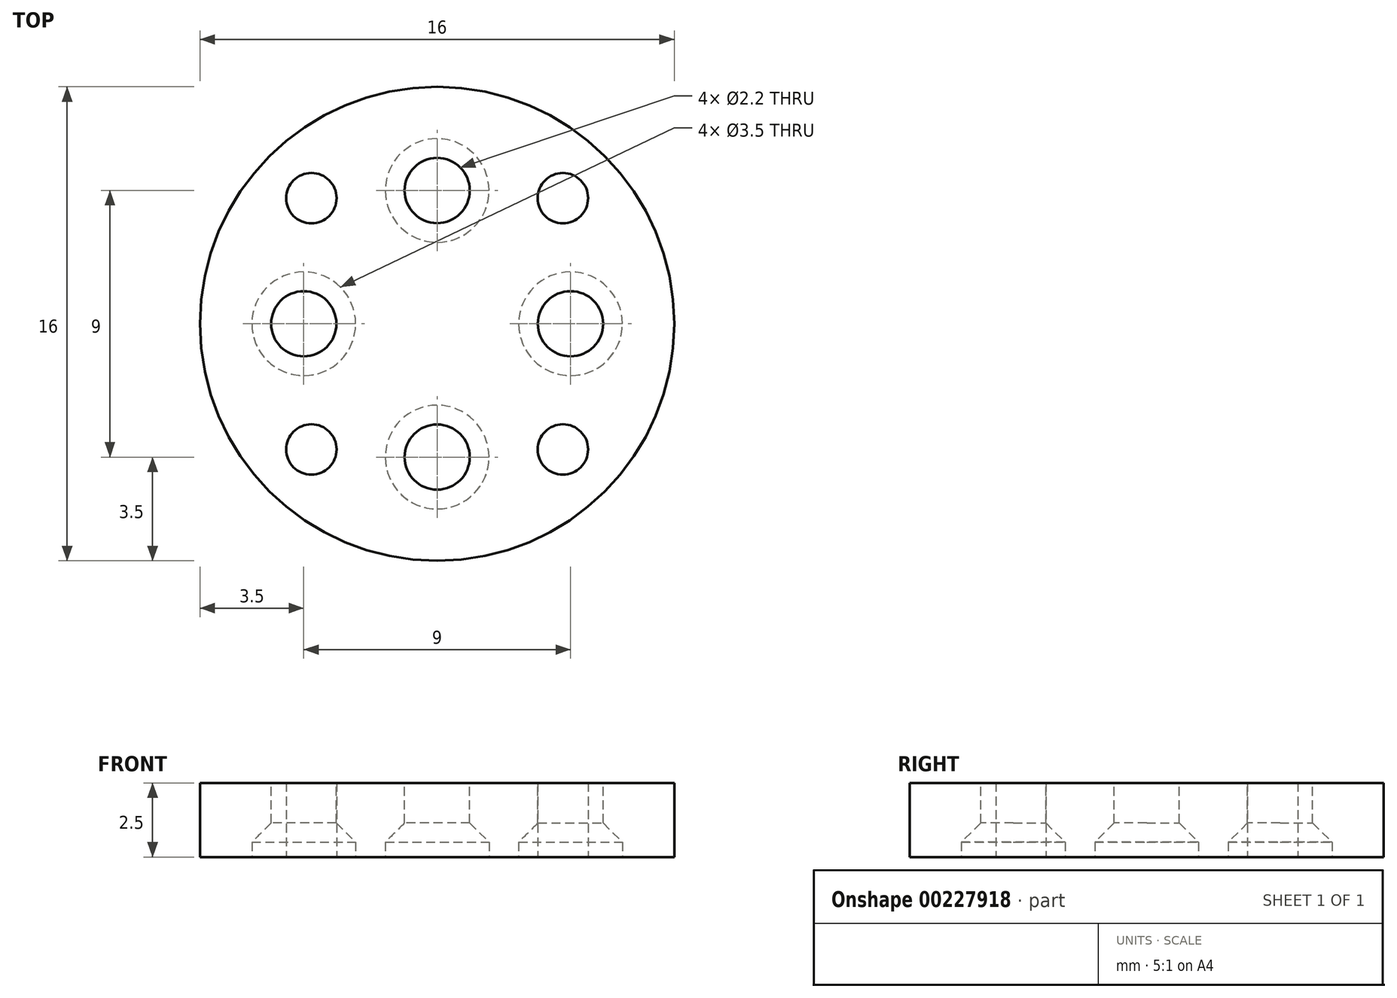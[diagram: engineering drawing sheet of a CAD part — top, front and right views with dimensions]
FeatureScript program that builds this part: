
annotation { "Feature Type Name" : "Feature", "Feature Type Description" : "" }
export const myFeature = defineFeature(function(context is Context, id is Id, definition is map)
    precondition{}
    {
        {
            var Q0;
            Q0=qCreatedBy(makeId("Top.planeOp"),FACE);
            var sketch = newSketch(context, id + "F0", { "sketchPlane" : qUnion([Q0])});
            skCircle(sketch, "E0", {"center": v(0, 0) * mm, "radius": 8 * mm});
            skSolve(sketch);
        }
        {
            var Q0;
            Q0=makeQuery(id+"F0.imprint","IMPRINT",FACE,{"disambiguationData":[TD([[makeQuery(id+"F0.imprint","IMPRINT",EDGE,{"derivedFrom":sQuery(id+"F0.wireOp",EDGE,"E0")}),1.0]])]});
            extrude(context, id + "F1", {"entities" : qUnion([Q0]), "depth" : 2.5 * mm});
        }
        {
            var Q0;
            Q0=makeQuery(id+"F1.opExtrude","CAP_FACE",FACE,{"disambiguationData":[OSD([sQuery(id+"F0.wireOp",EDGE,"E0")])],"isStart":false});
            var sketch = newSketch(context, id + "F2", { "sketchPlane" : qUnion([Q0])});
            skCircle(sketch, "E1", {"center": v(0, 4.5) * mm, "radius": 1.1 * mm});
            skCircle(sketch, "E2.1.0", {"center": v(-4.5, 0) * mm, "radius": 1.1 * mm});
            skCircle(sketch, "E2.2.0", {"center": v(0, -4.5) * mm, "radius": 1.1 * mm});
            skCircle(sketch, "E2.3.0", {"center": v(4.5, 0) * mm, "radius": 1.1 * mm});
            skPoint(sketch, "E2.center", {"position": v(0, 0) * mm});
            skSolve(sketch);
        }
        {
            var Q0;
            Q0 = qSketchRegion(id + "F2", true);
            extrude(context, id + "F3", {"entities" : qUnion([Q0]), "operationType" : NewBodyOperationType.REMOVE, "endBound" : BoundingType.THROUGH_ALL, "oppositeDirection" : true, "depth" : 25 * mm});
        }
        {
            var Q0;
            Q0=makeQuery(id+"F1.opExtrude","CAP_FACE",FACE,{"disambiguationData":[OSD([sQuery(id+"F0.wireOp",EDGE,"E0")])],"isStart":true});
            var sketch = newSketch(context, id + "F4", { "sketchPlane" : qUnion([Q0])});
            skCircle(sketch, "E3", {"center": v(4.24, 4.24) * mm, "radius": 0.85 * mm});
            skCircle(sketch, "E4.1.0", {"center": v(-4.24, 4.24) * mm, "radius": 0.85 * mm});
            skCircle(sketch, "E4.2.0", {"center": v(-4.24, -4.24) * mm, "radius": 0.85 * mm});
            skCircle(sketch, "E4.3.0", {"center": v(4.24, -4.24) * mm, "radius": 0.85 * mm});
            skPoint(sketch, "E4.center", {"position": v(0, 0) * mm});
            skLineSegment(sketch, "E5", {"start": v(0, 0) * mm, "end": v(4.24, 4.24) * mm, "construction": true});
            skSolve(sketch);
        }
        {
            var Q0;
            Q0=makeQuery(id+"F4.imprint","IMPRINT",FACE,{"disambiguationData":[TD([[makeQuery(id+"F4.imprint","IMPRINT",EDGE,{"derivedFrom":sQuery(id+"F4.wireOp",EDGE,"E4.1.0")}),1.0]])]});
            var Q1;
            Q1=makeQuery(id+"F4.imprint","IMPRINT",FACE,{"disambiguationData":[TD([[makeQuery(id+"F4.imprint","IMPRINT",EDGE,{"derivedFrom":sQuery(id+"F4.wireOp",EDGE,"E3")}),1.0]])]});
            var Q2;
            Q2=makeQuery(id+"F4.imprint","IMPRINT",FACE,{"disambiguationData":[TD([[makeQuery(id+"F4.imprint","IMPRINT",EDGE,{"derivedFrom":sQuery(id+"F4.wireOp",EDGE,"E4.3.0")}),1.0]])]});
            var Q3;
            Q3=makeQuery(id+"F4.imprint","IMPRINT",FACE,{"disambiguationData":[TD([[makeQuery(id+"F4.imprint","IMPRINT",EDGE,{"derivedFrom":sQuery(id+"F4.wireOp",EDGE,"E4.2.0")}),1.0]])]});
            extrude(context, id + "F5", {"entities" : qUnion([Q0, Q1, Q2, Q3]), "operationType" : NewBodyOperationType.REMOVE, "endBound" : BoundingType.THROUGH_ALL, "oppositeDirection" : true, "depth" : 25 * mm});
        }
        {
            var Q0;
            Q0=makeQuery(id+"F1.opExtrude","CAP_FACE",FACE,{"disambiguationData":[OSD([sQuery(id+"F0.wireOp",EDGE,"E0")])],"isStart":false});
            var sketch = newSketch(context, id + "F6", { "sketchPlane" : qUnion([Q0])});
            skArc(sketch, "E6", {"start": v(-4.24, 2.4) * mm, "mid": v(-2.93, 2.93) * mm, "end": v(-2.4, 4.24) * mm});
            skLineSegment(sketch, "E7", {"start": v(-2.4, 7.63) * mm, "end": v(-2.4, 4.24) * mm});
            skLineSegment(sketch, "E8", {"start": v(-7.63, 2.4) * mm, "end": v(-4.24, 2.4) * mm});
            skLineSegment(sketch, "E9", {"start": v(-4.24, 4.24) * mm, "end": v(0, 0) * mm, "construction": true});
            skArc(sketch, "E10.0", {"start": v(-2.4, 7.63) * mm, "mid": v(-5.66, 5.66) * mm, "end": v(-7.63, 2.4) * mm});
            skLineSegment(sketch, "E11.1.0", {"start": v(-2.4, -7.63) * mm, "end": v(-2.4, -4.24) * mm});
            skArc(sketch, "E11.1.1", {"start": v(-7.63, -2.4) * mm, "mid": v(-5.66, -5.66) * mm, "end": v(-2.4, -7.63) * mm});
            skLineSegment(sketch, "E11.1.2", {"start": v(-7.63, -2.4) * mm, "end": v(-4.24, -2.4) * mm});
            skArc(sketch, "E11.1.3", {"start": v(-2.4, -4.24) * mm, "mid": v(-2.93, -2.93) * mm, "end": v(-4.24, -2.4) * mm});
            skLineSegment(sketch, "E11.2.0", {"start": v(7.63, -2.4) * mm, "end": v(4.24, -2.4) * mm});
            skArc(sketch, "E11.2.1", {"start": v(2.4, -7.63) * mm, "mid": v(5.66, -5.66) * mm, "end": v(7.63, -2.4) * mm});
            skLineSegment(sketch, "E11.2.2", {"start": v(2.4, -7.63) * mm, "end": v(2.4, -4.24) * mm});
            skArc(sketch, "E11.2.3", {"start": v(4.24, -2.4) * mm, "mid": v(2.93, -2.93) * mm, "end": v(2.4, -4.24) * mm});
            skLineSegment(sketch, "E11.3.0", {"start": v(2.4, 7.63) * mm, "end": v(2.4, 4.24) * mm});
            skArc(sketch, "E11.3.1", {"start": v(7.63, 2.4) * mm, "mid": v(5.66, 5.66) * mm, "end": v(2.4, 7.63) * mm});
            skLineSegment(sketch, "E11.3.2", {"start": v(7.63, 2.4) * mm, "end": v(4.24, 2.4) * mm});
            skArc(sketch, "E11.3.3", {"start": v(2.4, 4.24) * mm, "mid": v(2.93, 2.93) * mm, "end": v(4.24, 2.4) * mm});
            skSolve(sketch);
        }
        {
            var Q0;
            Q0=qCreatedBy(makeId("Top.planeOp"),FACE);
            var sketch = newSketch(context, id + "F7", { "sketchPlane" : qUnion([Q0])});
            skCircle(sketch, "E12", {"center": v(0, -4.5) * mm, "radius": 1.75 * mm});
            skCircle(sketch, "E13", {"center": v(0, 4.5) * mm, "radius": 1.75 * mm});
            skCircle(sketch, "E14", {"center": v(-4.5, 0) * mm, "radius": 1.75 * mm});
            skCircle(sketch, "E15", {"center": v(4.5, 0) * mm, "radius": 1.75 * mm});
            skSolve(sketch);
        }
        {
            var Q0;
            Q0 = qSketchRegion(id + "F7", true);
            extrude(context, id + "F8", {"entities" : qUnion([Q0]), "operationType" : NewBodyOperationType.REMOVE, "depth" : 0.5 * mm});
        }
        {
            var Q0;
            Q0=makeQuery(id+"F8.boolean.opBoolean","COPY",FACE,{"derivedFrom":makeQuery(id+"F8.opExtrude","CAP_FACE",FACE,{"disambiguationData":[OSD([sQuery(id+"F7.wireOp",EDGE,"E15")])],"isStart":false})});
            var sketch = newSketch(context, id + "F9", { "sketchPlane" : qUnion([Q0])});
            skCircle(sketch, "E16.0", {"center": v(0, 4.5) * mm, "radius": 1.75 * mm});
            skCircle(sketch, "E17.0", {"center": v(-4.5, 0) * mm, "radius": 1.75 * mm});
            skCircle(sketch, "E18.0", {"center": v(0, -4.5) * mm, "radius": 1.75 * mm});
            skCircle(sketch, "E19.0", {"center": v(4.5, 0) * mm, "radius": 1.75 * mm});
            skSolve(sketch);
        }
        {
            var Q0;
            Q0 = qSketchRegion(id + "F9", true);
            extrude(context, id + "F10", {"entities" : qUnion([Q0]), "operationType" : NewBodyOperationType.REMOVE, "oppositeDirection" : true, "depth" : 25 * mm, "hasDraft" : true, "draftAngle" : 45 * degree, "draftPullDirection" : true});
        }
    });
